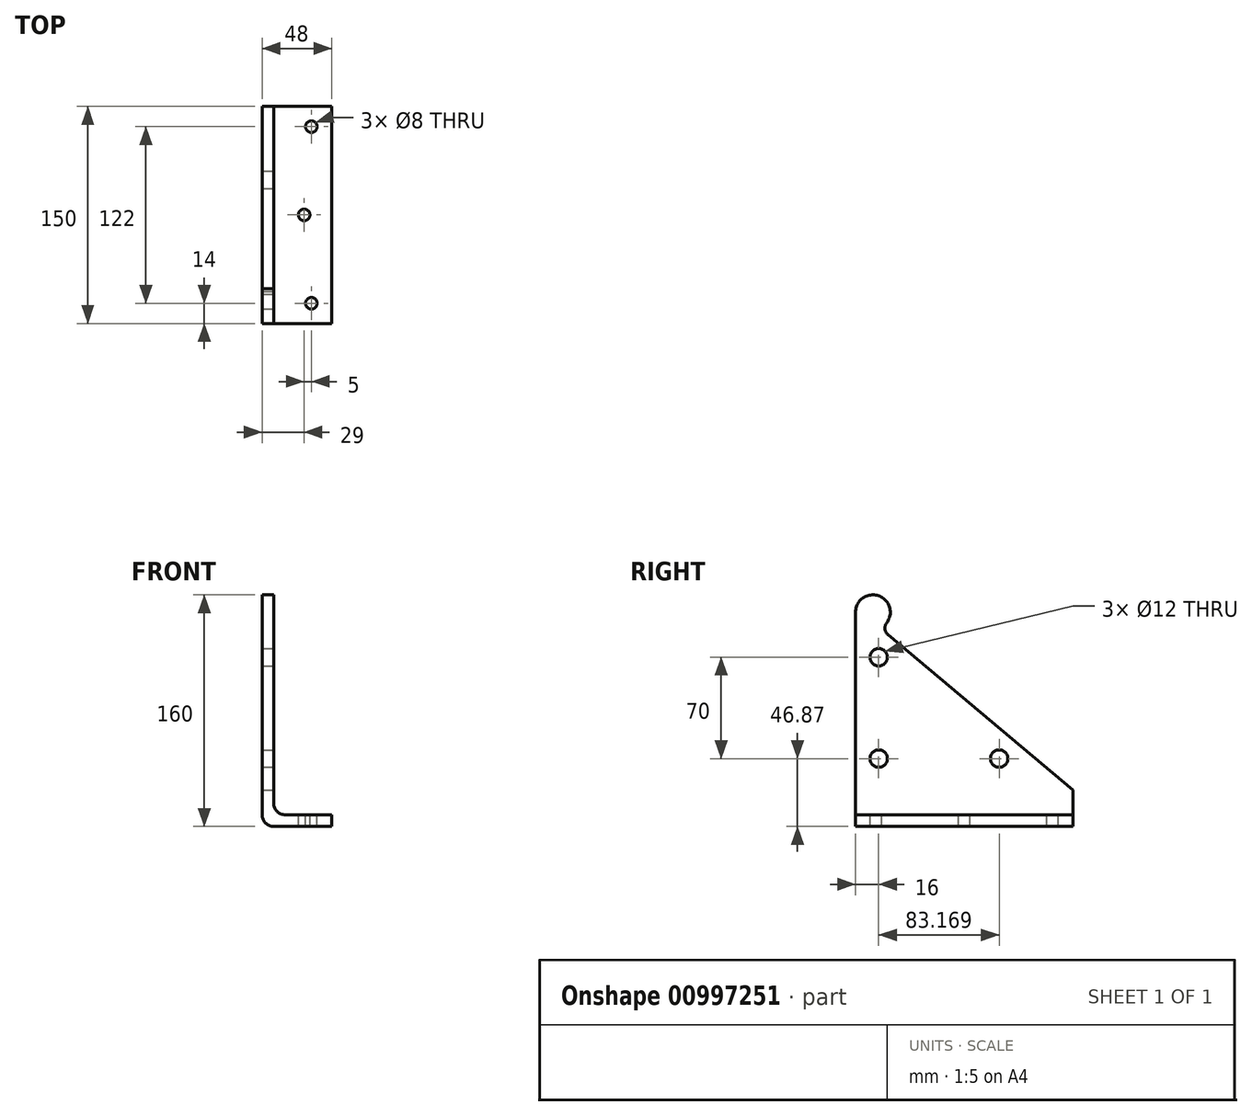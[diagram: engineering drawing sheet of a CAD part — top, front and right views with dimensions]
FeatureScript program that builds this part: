
annotation { "Feature Type Name" : "Feature", "Feature Type Description" : "" }
export const myFeature = defineFeature(function(context is Context, id is Id, definition is map)
    precondition{}
    {
        {
            var Q0;
            Q0=qCreatedBy(makeId("Front.planeOp"),FACE);
            var sketch = newSketch(context, id + "F0", { "sketchPlane" : qUnion([Q0])});
            skLineSegment(sketch, "E0", {"start": v(-4, 80) * mm, "end": v(-4, -80) * mm});
            skLineSegment(sketch, "E1", {"start": v(-4, -80) * mm, "end": v(44, -80) * mm});
            skLineSegment(sketch, "E2", {"start": v(44, -80) * mm, "end": v(44, -72) * mm});
            skLineSegment(sketch, "E3", {"start": v(44, -72) * mm, "end": v(4, -72) * mm});
            skLineSegment(sketch, "E4", {"start": v(4, -72) * mm, "end": v(4, 80) * mm});
            skLineSegment(sketch, "E5", {"start": v(4, 80) * mm, "end": v(-4, 80) * mm});
            skSolve(sketch);
        }
        {
            var Q0;
            Q0 = qSketchRegion(id + "F0", true);
            extrude(context, id + "F1", {"entities" : qUnion([Q0]), "endBound" : BoundingType.SYMMETRIC, "depth" : 150 * mm, "offsetDistance" : 25 * mm});
        }
        {
            var Q0;
            Q0=makeQuery(id+"F1.opExtrude","SWEPT_EDGE",EDGE,{"disambiguationData":[OSD([sQuery(id+"F0.wireOp",EDGE,"E3"),sQuery(id+"F0.wireOp",EDGE,"E4")])]});
            var Q1;
            Q1=makeQuery(id+"F1.opExtrude","SWEPT_EDGE",EDGE,{"disambiguationData":[OSD([sQuery(id+"F0.wireOp",EDGE,"E0"),sQuery(id+"F0.wireOp",EDGE,"E1")])]});
            fillet(context, id + "F2", {"entities" : qUnion([Q0, Q1]), "radius" : 8 * mm, "tangentPropagation" : true, "allowEdgeOverflow" : false});
        }
        {
            var Q0;
            Q0=makeQuery(id+"F1.opExtrude","SWEPT_FACE",FACE,{"disambiguationData":[OSD([sQuery(id+"F0.wireOp",EDGE,"E4")])]});
            var sketch = newSketch(context, id + "F3", { "sketchPlane" : qUnion([Q0])});
            skCircle(sketch, "E6", {"center": v(-63, 68) * mm, "radius": 12 * mm});
            skArc(sketch, "E7", {"start": v(-53.5, 60.67) * mm, "mid": v(-54.72, 56.36) * mm, "end": v(-52.62, 52.4) * mm});
            skLineSegment(sketch, "E8", {"start": v(75, -55) * mm, "end": v(-52.62, 52.4) * mm});
            skLineSegment(sketch, "E9", {"start": v(-63, 80) * mm, "end": v(75, 80) * mm});
            skLineSegment(sketch, "E10", {"start": v(75, 80) * mm, "end": v(75, -55) * mm});
            skCircle(sketch, "E11", {"center": v(-59, 36.87) * mm, "radius": 6 * mm});
            skCircle(sketch, "E12", {"center": v(-59, -33.13) * mm, "radius": 6 * mm});
            skCircle(sketch, "E13", {"center": v(24.17, -33.13) * mm, "radius": 6 * mm});
            skSolve(sketch);
        }
        {
            var Q0;
            {var subQ1=sQuery(id+"F3.wireOp",EDGE,"E7");Q0=makeQuery(id+"F3.imprint","IMPRINT",FACE,{"disambiguationData":[TD([[makeQuery(id+"F3.imprint","IMPRINT",EDGE,{"derivedFrom":subQ1}),1.0]])]});}
            var Q1;
            {var subQ0=sQuery(id+"F3.wireOp",EDGE,"E6");var subQ1=sQuery(id+"F0.wireOp",EDGE,"E4");var subQ4=makeQuery(id+"F1.opExtrude","CAP_EDGE",EDGE,{"disambiguationData":[OSD([subQ1])],"isStart":false});var subQ5=makeQuery(id+"F3.imprint","INTERSECT",VERTEX,{"derivedFrom":[subQ4,subQ0]});Q1=makeQuery(id+"F3.imprint","IMPRINT",FACE,{"disambiguationData":[TD([[makeQuery(id+"F3.imprint","IMPRINT",EDGE,{"disambiguationData":[TD([[subQ5,-1.0]])],"derivedFrom":subQ4}),-1.0]])]});}
            var Q2;
            Q2=makeQuery(id+"F3.imprint","IMPRINT",FACE,{"disambiguationData":[TD([[makeQuery(id+"F3.imprint","IMPRINT",EDGE,{"derivedFrom":sQuery(id+"F3.wireOp",EDGE,"E11")}),1.0]])]});
            var Q3;
            Q3=makeQuery(id+"F3.imprint","IMPRINT",FACE,{"disambiguationData":[TD([[makeQuery(id+"F3.imprint","IMPRINT",EDGE,{"derivedFrom":sQuery(id+"F3.wireOp",EDGE,"E12")}),1.0]])]});
            var Q4;
            Q4=makeQuery(id+"F3.imprint","IMPRINT",FACE,{"disambiguationData":[TD([[makeQuery(id+"F3.imprint","IMPRINT",EDGE,{"derivedFrom":sQuery(id+"F3.wireOp",EDGE,"E13")}),1.0]])]});
            extrude(context, id + "F4", {"entities" : qUnion([Q0, Q1, Q2, Q3, Q4]), "operationType" : NewBodyOperationType.REMOVE, "endBound" : BoundingType.THROUGH_ALL, "oppositeDirection" : true, "depth" : 25 * mm, "offsetDistance" : 25 * mm});
        }
        {
            var Q0;
            Q0=qCreatedBy(makeId("Top.planeOp"),FACE);
            var sketch = newSketch(context, id + "F5", { "sketchPlane" : qUnion([Q0])});
            skCircle(sketch, "E14", {"center": v(30, -61) * mm, "radius": 4 * mm});
            skCircle(sketch, "E15", {"center": v(25, 0) * mm, "radius": 4 * mm});
            skCircle(sketch, "E16", {"center": v(30, 61) * mm, "radius": 4 * mm});
            skSolve(sketch);
        }
        {
            var Q0;
            Q0 = qSketchRegion(id + "F5", true);
            extrude(context, id + "F6", {"entities" : qUnion([Q0]), "operationType" : NewBodyOperationType.REMOVE, "endBound" : BoundingType.THROUGH_ALL, "oppositeDirection" : true, "depth" : 0 * mm, "offsetDistance" : 25 * mm});
        }
    });
